# Revit family: ACW-B
name_source: partatom
category: Mechanical Equipment
units: mm (PartAtom-declared; Revit-internal decimal feet)

## family parameters
Always vertical = Yes
Cut with Voids When Loaded = No
Part Type = Normal
Room Calculation Point = No
Round Connector Dimension = Use Radius
Shared = No
Work Plane-Based = No

## types (23) — shared parameters
0 = 0"
1" = 1"
1.5 = 1 1/2"
2" = 2"
2' = 24"
3" = 3"
4" = 4"
45 = 45.00°
G = 1/2"
G/2 = 0"
H = 4"
HOLES = Yes
Manufacturer = Loren Cook Company
ONE EIGTH = 0"
Type Comments = Centrifugal Exhaust Ventilator Wall Mounted/Belt Drive
URL = www.lorencook.com

## per-type parameters (varying)
| type | ((B/2-E/2)*.3)+(E/2) | A | A/2 | B | B/2 | C | C/2 | E_ROUND | E_ROUND/2 | E_SQ | F | F/2 | Model | T | T/2 |
| 100_ACW-B | 7 1/2" | 13" | 6 1/2" | 25" | 12 1/2" | 21 1/2" | 10 1/2" | 10" | 5" | 10" | 20" | 10" | ACW-B | 21 1/2" | 10 1/2" |
| 120_ACW-B | 8 1/2" | 18 1/2" | 9" | 30" | 15" | 26 1/2" | 13" | 12" | 6" | 12" | 23 1/2" | 12" | ACW-B | 25" | 12 1/2" |
| 135_ACW-B | 8 1/2" | 18 1/2" | 9" | 30" | 15" | 29" | 14 1/2" | 12" | 6" | 12" | 23 1/2" | 12" | ACW-B | 25" | 12 1/2" |
| 150_ACW-B | 10" | 20" | 10" | 34 1/2" | 17 1/2" | 30 1/2" | 15" | 14" | 7" | 16" | 28 1/2" | 14 1/2" | ACW-B | 30" | 15" |
| 165_ACW-B | 10" | 20" | 10" | 34 1/2" | 17 1/2" | 31" | 15 1/2" | 14" | 7" | 16" | 28 1/2" | 14 1/2" | ACW-B | 30" | 15" |
| 180_ACW-B | 12" | 22 1/2" | 11 1/2" | 39 1/2" | 19 1/2" | 35 1/2" | 18" | 18" | 9" | 20" | 34 1/2" | 17 1/2" | ACW-B | 36" | 18" |
| 195_ACW-B | 13 1/2" | 22 1/2" | 11 1/2" | 39 1/2" | 19 1/2" | 36" | 18" | 22" | 11" | 20" | 34 1/2" | 17 1/2" | ACW-B | 36" | 18" |
| 210_ACW-B | 14 1/2" | 23 1/2" | 12" | 45 1/2" | 22 1/2" | 38" | 19" | 22" | 11" | 24" | 39 1/2" | 20" | ACW-B | 41" | 20 1/2" |
| 225_ACW-B | 14 1/2" | 23 1/2" | 12" | 45 1/2" | 22 1/2" | 38 1/2" | 19" | 22" | 11" | 24" | 39 1/2" | 20" | ACW-B | 41" | 20 1/2" |
| 245_ACW-B | 15" | 25 1/2" | 12 1/2" | 49 1/2" | 24 1/2" | 40" | 20" | 22" | 11" | 24" | 43 1/2" | 22" | ACW-B | 45" | 22 1/2" |
| 150_ACW-HP | 10" | 20" | 10" | 34 1/2" | 17 1/2" | 27 1/2" | 14" | 14" | 7" | 16" | 28 1/2" | 14 1/2" | ACW-HP | 30" | 15" |
| 165_ACW-HP | 10" | 20" | 10" | 34 1/2" | 17 1/2" | 28" | 14" | 14" | 7" | 16" | 28 1/2" | 14 1/2" | ACW-HP | 30" | 15" |
| 180_ACW-HP | 12" | 22 1/2" | 11 1/2" | 39 1/2" | 19 1/2" | 33" | 16 1/2" | 18" | 9" | 20" | 34 1/2" | 17 1/2" | ACW-HP | 36" | 18" |
| 195_ACW-HP | 13 1/2" | 22 1/2" | 11 1/2" | 39 1/2" | 19 1/2" | 33 1/2" | 16 1/2" | 22" | 11" | 20" | 34 1/2" | 17 1/2" | ACW-HP | 36" | 18" |
| 210_ACW-HP | 14 1/2" | 23 1/2" | 12" | 45 1/2" | 22 1/2" | 35" | 17 1/2" | 22" | 11" | 24" | 39 1/2" | 20" | ACW-HP | 41" | 20 1/2" |
| 225_ACW-HP | 14 1/2" | 23 1/2" | 12" | 45 1/2" | 22 1/2" | 35 1/2" | 18" | 22" | 11" | 24" | 39 1/2" | 20" | ACW-HP | 41" | 20 1/2" |
| 245_ACW-HP | 15" | 25 1/2" | 12 1/2" | 49 1/2" | 24 1/2" | 36" | 18" | 22" | 11" | 24" | 43 1/2" | 22" | ACW-HP | 45" | 22 1/2" |
| 165_ACW-XP | 10" | 20" | 10" | 34 1/2" | 17 1/2" | 27" | 13 1/2" | 14" | 7" | 16" | 28 1/2" | 14 1/2" | ACW-XP | 30" | 15" |
| 180_ACW-XP | 12" | 22 1/2" | 11 1/2" | 39 1/2" | 19 1/2" | 31 1/2" | 15 1/2" | 18" | 9" | 20" | 34 1/2" | 17 1/2" | ACW-XP | 36" | 18" |
| 195_ACW-XP | 13 1/2" | 22 1/2" | 11 1/2" | 39 1/2" | 19 1/2" | 32" | 16" | 22" | 11" | 20" | 34 1/2" | 17 1/2" | ACW-XP | 36" | 18" |
| 210_ACW-XP | 14 1/2" | 23 1/2" | 12" | 45 1/2" | 22 1/2" | 32" | 16" | 22" | 11" | 24" | 39 1/2" | 20" | ACW-XP | 41" | 20 1/2" |
| 225_ACW-XP | 14 1/2" | 23 1/2" | 12" | 45 1/2" | 22 1/2" | 33 1/2" | 16 1/2" | 22" | 11" | 24" | 39 1/2" | 20" | ACW-XP | 41" | 20 1/2" |
| 245_ACW-XP | 15" | 25 1/2" | 12 1/2" | 49 1/2" | 24 1/2" | 33" | 16 1/2" | 22" | 11" | 24" | 43 1/2" | 22" | ACW-XP | 45" | 22 1/2" |

## geometry (parser evidence)
native form markers: Sweep x1
no freeform markers — native parametric forms only
